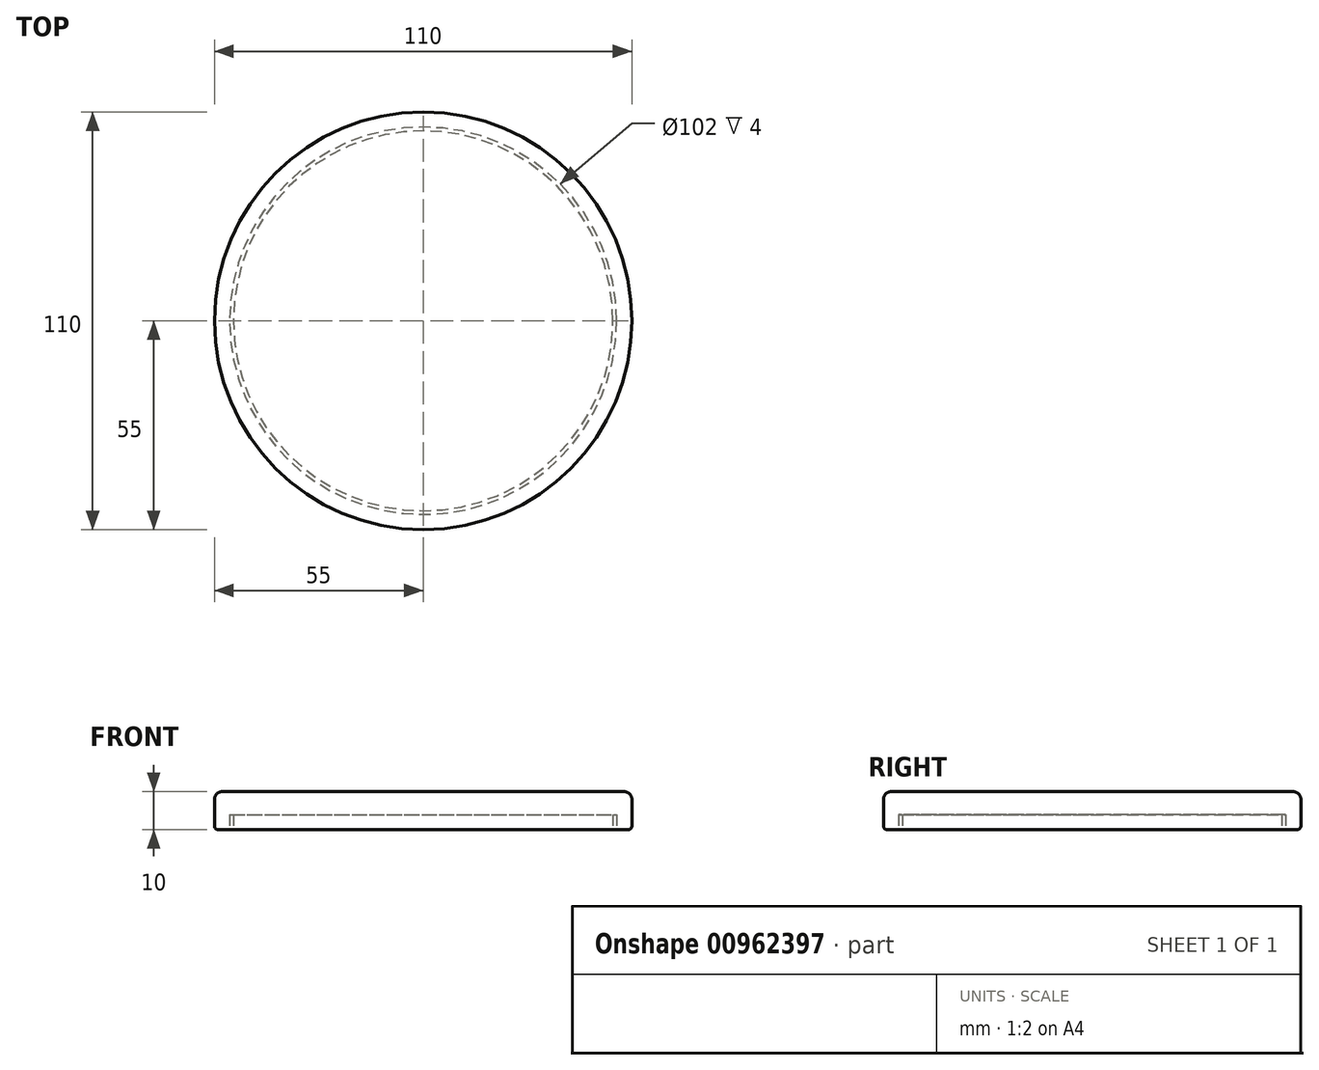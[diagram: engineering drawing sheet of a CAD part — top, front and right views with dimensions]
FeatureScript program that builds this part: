
annotation { "Feature Type Name" : "Feature", "Feature Type Description" : "" }
export const myFeature = defineFeature(function(context is Context, id is Id, definition is map)
    precondition{}
    {
        {
            var Q0;
            Q0=qCreatedBy(makeId("Top.planeOp"),FACE);
            var sketch = newSketch(context, id + "F0", { "sketchPlane" : qUnion([Q0])});
            skCircle(sketch, "E0", {"center": v(0, 0) * mm, "radius": 55 * mm});
            skSolve(sketch);
        }
        {
            var Q0;
            Q0=makeQuery(id+"F0.imprint","IMPRINT",FACE,{"disambiguationData":[TD([[makeQuery(id+"F0.imprint","IMPRINT",EDGE,{"derivedFrom":sQuery(id+"F0.wireOp",EDGE,"E0")}),1.0]])]});
            extrude(context, id + "F1", {"entities" : qUnion([Q0]), "depth" : 10 * mm, "offsetDistance" : 25 * mm});
        }
        {
            var Q0;
            Q0=makeQuery(id+"F1.opExtrude","CAP_EDGE",EDGE,{"disambiguationData":[OSD([sQuery(id+"F0.wireOp",EDGE,"E0")])],"isStart":true});
            fillet(context, id + "F2", {"entities" : qUnion([Q0]), "radius" : 1 * mm, "tangentPropagation" : true, "allowEdgeOverflow" : false});
        }
        {
            var Q0;
            Q0=makeQuery(id+"F1.opExtrude","CAP_FACE",FACE,{"disambiguationData":[OSD([sQuery(id+"F0.wireOp",EDGE,"E0"),sQuery(id+"F0.wireOp",EDGE,"dpFjTfjf-PTI8-wQmo-9to0-mpq3u57dXHyD"),sQuery(id+"F0.wireOp",EDGE,"KZ98ytGi-FkMO-cLRg-SQhK-xACwNeptLR8x")])],"isStart":true});
            var sketch = newSketch(context, id + "F3", { "sketchPlane" : qUnion([Q0])});
            skCircle(sketch, "E1", {"center": v(0, 0) * mm, "radius": 51 * mm});
            skCircle(sketch, "E2", {"center": v(0, 0) * mm, "radius": 50 * mm});
            skCircle(sketch, "E3", {"center": v(-32.16, 0) * mm, "radius": 1.4 * mm});
            skCircle(sketch, "E4", {"center": v(6, 29.1) * mm, "radius": 1.4 * mm});
            skCircle(sketch, "E5", {"center": v(4.83, -37.8) * mm, "radius": 1.4 * mm});
            skCircle(sketch, "E6", {"center": v(26.11, -19.93) * mm, "radius": 1.4 * mm});
            skSolve(sketch);
        }
        {
            var Q0;
            Q0=makeQuery(id+"F3.imprint","IMPRINT",FACE,{"disambiguationData":[TD([[makeQuery(id+"F3.imprint","IMPRINT",EDGE,{"derivedFrom":sQuery(id+"F3.wireOp",EDGE,"E1")}),1.0]])]});
            extrude(context, id + "F4", {"entities" : qUnion([Q0]), "operationType" : NewBodyOperationType.REMOVE, "oppositeDirection" : true, "depth" : 4 * mm, "offsetDistance" : 25 * mm});
        }
        {
            var Q0;
            Q0=makeQuery(id+"F1.opExtrude","CAP_EDGE",EDGE,{"disambiguationData":[OSD([sQuery(id+"F0.wireOp",EDGE,"E0")])],"isStart":false});
            fillet(context, id + "F5", {"entities" : qUnion([Q0]), "radius" : 2 * mm, "tangentPropagation" : true, "allowEdgeOverflow" : false});
        }
    });
